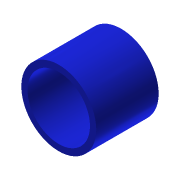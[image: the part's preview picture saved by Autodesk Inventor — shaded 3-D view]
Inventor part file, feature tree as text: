
AUTODESK INVENTOR PART (.ipt)
format: ipt  version: 2016 (Build 200138000, 138)  size: 83,456 bytes
history: native  units: in
note: dims shown in document units (in); Inventor stores cm internally (conversion verified against a paired STEP export)
features: extrude x1, sketch x1
ambient origin geometry x8: Origin, YZ Plane, XZ Plane, XY Plane, X Axis, Y Axis, Z Axis, Center Point
bodies: Solid1 (feature_tree)
feature tree (2):
  extrude  "Extrusion1"  Depth=0.3937in
  sketch  "Sketch1"  dims[d0=0.3937in d1=0.4724in d2=0.3937in d3=0.0in]
